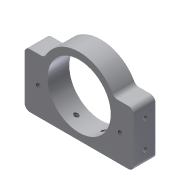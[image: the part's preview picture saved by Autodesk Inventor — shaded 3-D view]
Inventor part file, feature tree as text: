
AUTODESK INVENTOR PART (.ipt)
format: ipt  version: 2013 (Build 170138000, 138)  size: 157,184 bytes
history: native  units: in
note: dims shown in document units (in); Inventor stores cm internally (conversion verified against a paired STEP export)
features: sketch x4, hole x3, projected_geometry x2, extrude x1, fillet x1, mirror x1
ambient origin geometry x8: Origin, YZ Plane, XZ Plane, XY Plane, X Axis, Y Axis, Z Axis, Center Point
bodies: Solid1 (feature_tree)
feature tree (12):
  extrude  "Extrusion1"  Depth=0.8858in
  fillet  "Fillet1"  Radius=2.5197in
  hole  "Hole1"  [1 undecoded]
  hole  "Hole2"  [1 undecoded]
  mirror  "Mirror1"
  hole  "Hole3"  [1 undecoded]
  sketch  "Sketch1"  dims[d0=1.4567in d1=0.8858in d2=2.5197in]
  sketch  "Sketch2"  dims[d3=0.8858in d4=1.2598in]
  projected_geometry  "Projected Loop1"
  sketch  "Sketch4"  dims[d5=0.5in d6=0.0in d7=0.125in]
  projected_geometry  "Projected Loop3"
  sketch  "Sketch5"  dims[d8=0.6299in d11=0.315in d12=0.104in d13=0.75in d14=0.375in d15=0.25in d16=0.5635in d17=0.4375in d18=0.8108in d19=0.6299in d23=1.2598in d24=0.6299in d25=0.104in d26=0.75in d27=0.375in d28=0.25in d29=0.5635in d30=0.4375in d31=0.8108in d32=1.8898in d34=0.9449in d35=0.6299in d36=0.104in d37=0.75in d38=0.375in d39=0.25in d40=0.5635in d41=1.0in d42=0.8108in d43=0.6299in d44=0.6299in]
note: 3 required parameter values undecoded (feature->parameter linkage not recoverable at this tier; creation-order binding heuristic only, values carry confidence <= 0.55)
